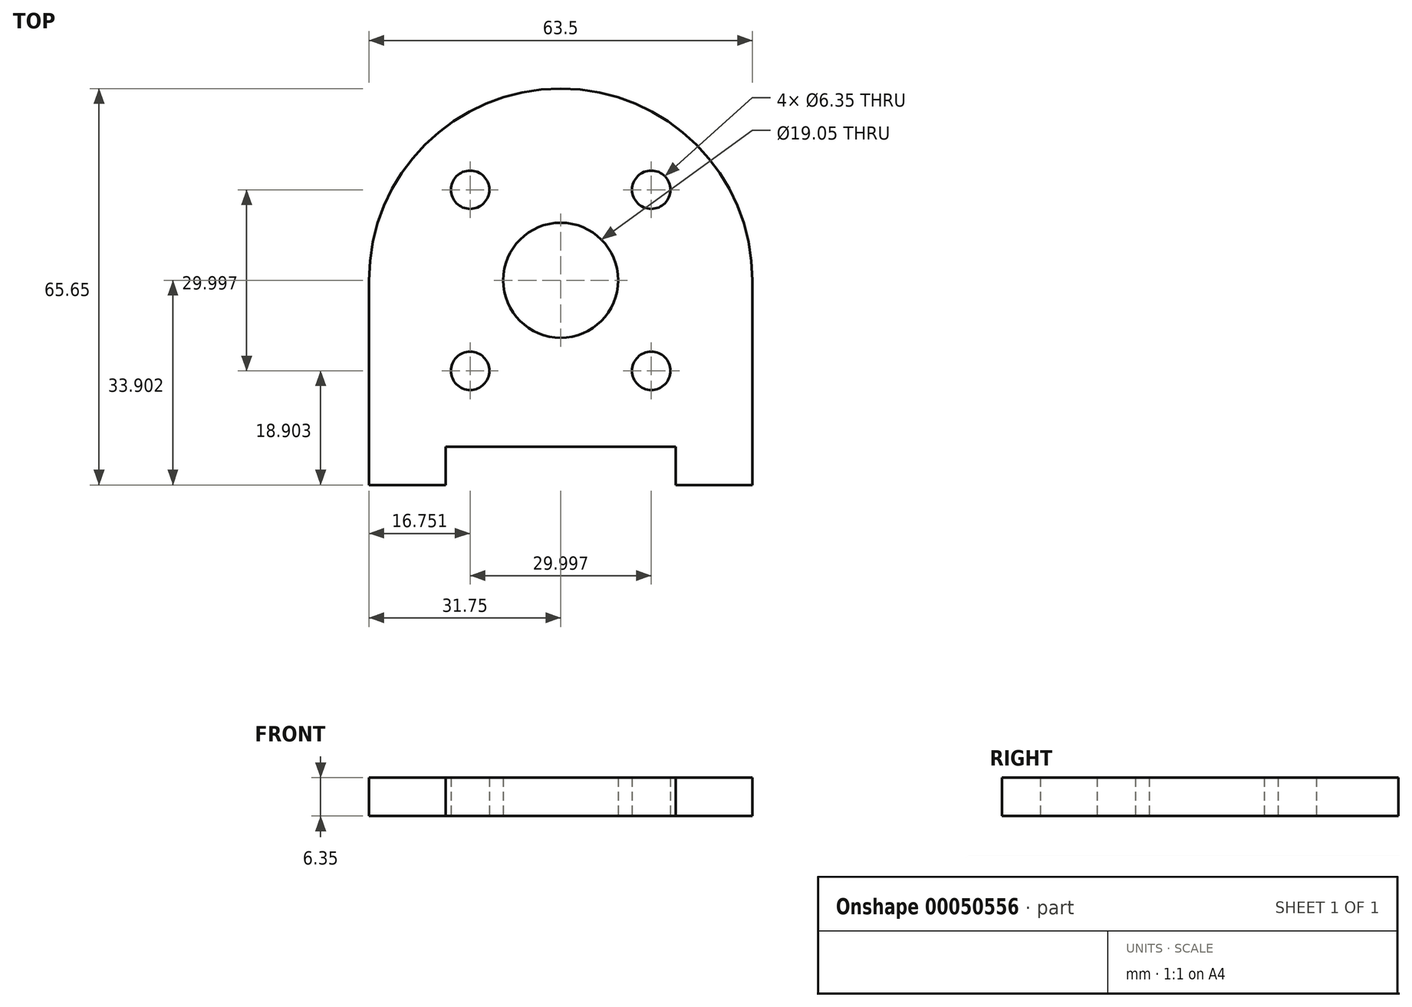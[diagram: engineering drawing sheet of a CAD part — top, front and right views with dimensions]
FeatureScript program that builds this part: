
annotation { "Feature Type Name" : "Feature", "Feature Type Description" : "" }
export const myFeature = defineFeature(function(context is Context, id is Id, definition is map)
    precondition{}
    {
        {
            var Q0;
            Q0=qCreatedBy(makeId("Top.planeOp"),FACE);
            var sketch = newSketch(context, id + "F0", { "sketchPlane" : qUnion([Q0])});
            skLineSegment(sketch, "E0.rect.top", {"start": v(31.75, 16.95) * mm, "end": v(-31.75, 16.95) * mm});
            skLineSegment(sketch, "E0.rect.left", {"start": v(31.75, -16.95) * mm, "end": v(31.75, 16.95) * mm});
            skLineSegment(sketch, "E0.rect.right", {"start": v(-31.75, -16.95) * mm, "end": v(-31.75, 16.95) * mm});
            skPoint(sketch, "E0.rect.middle", {"position": v(0, 0) * mm});
            skArc(sketch, "E1", {"start": v(-31.75, 16.95) * mm, "mid": v(0, 48.7) * mm, "end": v(31.75, 16.95) * mm});
            skLineSegment(sketch, "E2", {"start": v(-61.9, 16.95) * mm, "end": v(0, 16.95) * mm, "construction": true});
            skLineSegment(sketch, "E3", {"start": v(0, 78.86) * mm, "end": v(0, 16.95) * mm, "construction": true});
            skCircle(sketch, "E4", {"center": v(-15, 31.95) * mm, "radius": 3.18 * mm});
            skCircle(sketch, "E5.MirrorC", {"center": v(15, 31.95) * mm, "radius": 3.18 * mm});
            skCircle(sketch, "E6.MirrorC", {"center": v(-15, 1.95) * mm, "radius": 3.18 * mm});
            skCircle(sketch, "E7.MirrorC", {"center": v(15, 1.95) * mm, "radius": 3.18 * mm});
            skLineSegment(sketch, "E8", {"start": v(-15, 31.95) * mm, "end": v(15, 31.95) * mm, "construction": true});
            skLineSegment(sketch, "E9", {"start": v(-15, 31.95) * mm, "end": v(-15, 1.95) * mm, "construction": true});
            skCircle(sketch, "E10", {"center": v(0, 16.95) * mm, "radius": 9.53 * mm});
            skLineSegment(sketch, "E11", {"start": v(-31.75, 5.72) * mm, "end": v(31.75, 5.72) * mm, "construction": true});
            skLineSegment(sketch, "E12", {"start": v(-31.75, -16.95) * mm, "end": v(-19.05, -16.95) * mm});
            skLineSegment(sketch, "E13", {"start": v(-19.05, -16.95) * mm, "end": v(-19.05, -10.6) * mm});
            skLineSegment(sketch, "E14", {"start": v(-19.05, -10.6) * mm, "end": v(19.05, -10.6) * mm});
            skLineSegment(sketch, "E15", {"start": v(19.05, -10.6) * mm, "end": v(19.05, -16.95) * mm});
            skLineSegment(sketch, "E16", {"start": v(19.05, -16.95) * mm, "end": v(31.75, -16.95) * mm});
            skSolve(sketch);
        }
        {
            var Q0;
            Q0 = qSketchRegion(id + "F0", true);
            extrude(context, id + "F1", {"entities" : qUnion([Q0]), "depth" : 6.35 * mm});
        }
    });
